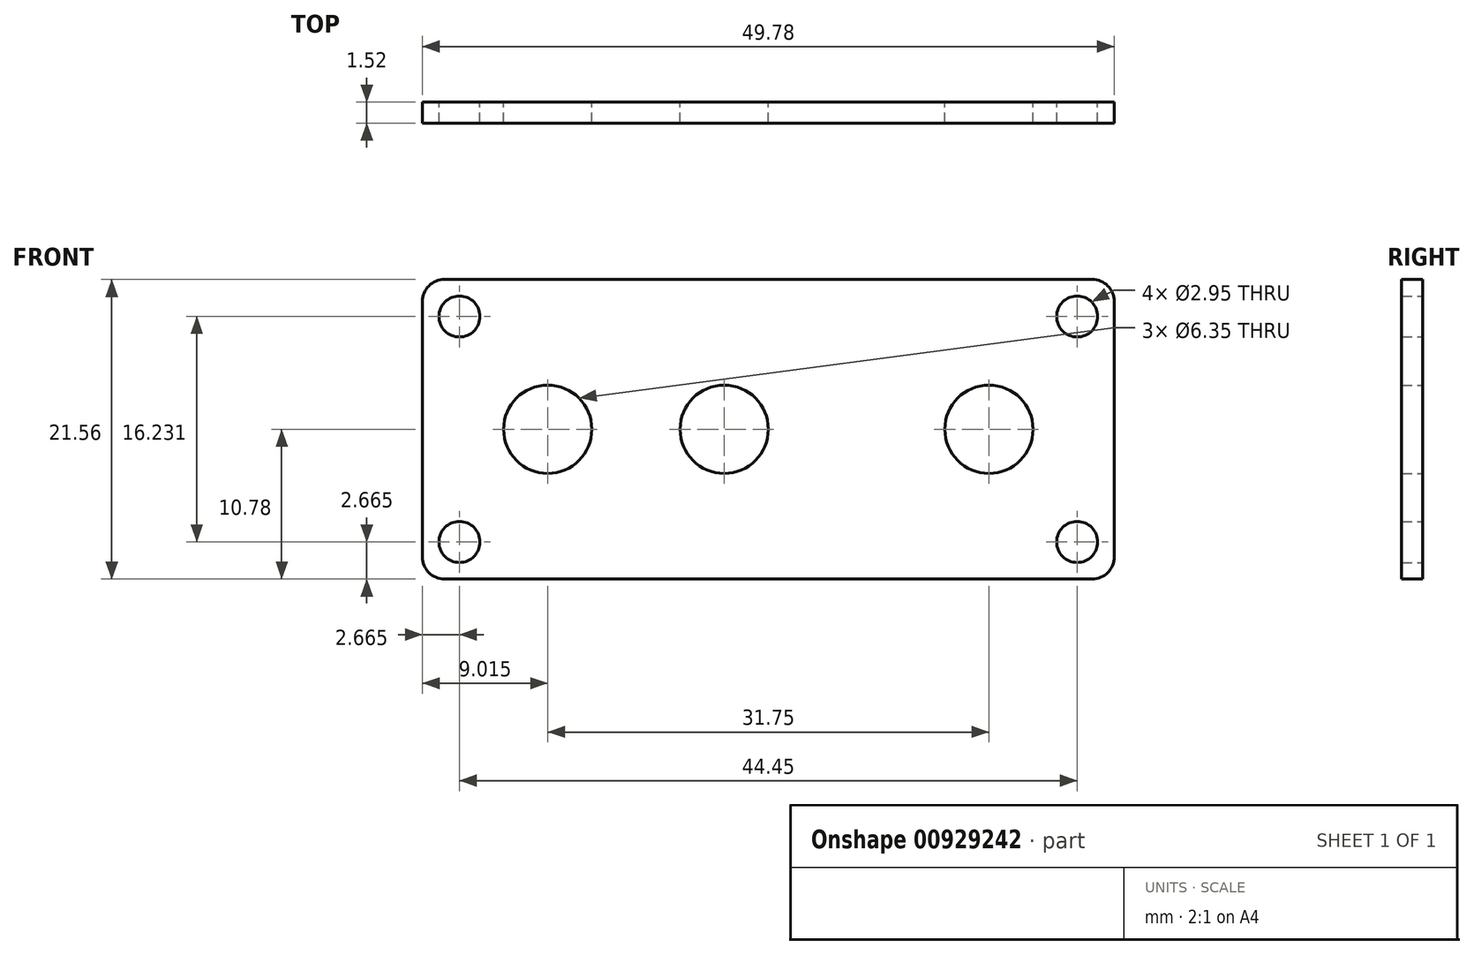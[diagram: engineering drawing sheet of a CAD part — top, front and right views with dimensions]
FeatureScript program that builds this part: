
annotation { "Feature Type Name" : "Feature", "Feature Type Description" : "" }
export const myFeature = defineFeature(function(context is Context, id is Id, definition is map)
    precondition{}
    {
        {
            var Q0;
            Q0=qCreatedBy(makeId("Front.planeOp"),FACE);
            var sketch = newSketch(context, id + "F0", { "sketchPlane" : qUnion([Q0])});
            skLineSegment(sketch, "E0.bottom", {"start": v(-23.3, 10.78) * mm, "end": v(23.3, 10.78) * mm});
            skLineSegment(sketch, "E0.top", {"start": v(-23.3, -10.78) * mm, "end": v(23.3, -10.78) * mm});
            skLineSegment(sketch, "E0.left", {"start": v(-24.9, 9.2) * mm, "end": v(-24.9, -9.2) * mm});
            skLineSegment(sketch, "E0.right", {"start": v(24.9, 9.2) * mm, "end": v(24.9, -9.2) * mm});
            skPoint(sketch, "E0.middle", {"position": v(0, 0) * mm});
            skPoint(sketch, "E1.visualSharp", {"position": v(24.9, 10.78) * mm});
            skArc(sketch, "E1.filletArc", {"start": v(24.9, 9.2) * mm, "mid": v(24.43, 10.32) * mm, "end": v(23.3, 10.78) * mm});
            skPoint(sketch, "E2.visualSharp", {"position": v(-24.9, 10.78) * mm});
            skArc(sketch, "E2.filletArc", {"start": v(-23.3, 10.78) * mm, "mid": v(-24.43, 10.32) * mm, "end": v(-24.9, 9.2) * mm});
            skPoint(sketch, "E3.visualSharp", {"position": v(-24.9, -10.78) * mm});
            skArc(sketch, "E3.filletArc", {"start": v(-24.9, -9.2) * mm, "mid": v(-24.43, -10.32) * mm, "end": v(-23.3, -10.78) * mm});
            skPoint(sketch, "E4.visualSharp", {"position": v(24.9, -10.78) * mm});
            skArc(sketch, "E4.filletArc", {"start": v(23.3, -10.78) * mm, "mid": v(24.43, -10.32) * mm, "end": v(24.9, -9.2) * mm});
            skCircle(sketch, "E5", {"center": v(-15.88, 0) * mm, "radius": 3.18 * mm});
            skCircle(sketch, "E6", {"center": v(-3.17, 0) * mm, "radius": 3.18 * mm});
            skCircle(sketch, "E7", {"center": v(15.88, 0) * mm, "radius": 3.18 * mm});
            skCircle(sketch, "E8", {"center": v(-22.23, 8.12) * mm, "radius": 1.47 * mm});
            skCircle(sketch, "E9", {"center": v(22.23, 8.12) * mm, "radius": 1.47 * mm});
            skCircle(sketch, "E10", {"center": v(22.23, -8.12) * mm, "radius": 1.47 * mm});
            skCircle(sketch, "E11", {"center": v(-22.22, -8.12) * mm, "radius": 1.47 * mm});
            skSolve(sketch);
        }
        {
            var Q0;
            Q0=makeQuery(id+"F0.imprint","IMPRINT",FACE,{"disambiguationData":[TD([[makeQuery(id+"F0.imprint","IMPRINT",EDGE,{"derivedFrom":sQuery(id+"F0.wireOp",EDGE,"E0.bottom")}),-1.0]])]});
            extrude(context, id + "F1", {"entities" : qUnion([Q0]), "depth" : 1.52 * mm, "offsetDistance" : 25.4 * mm});
        }
    });
